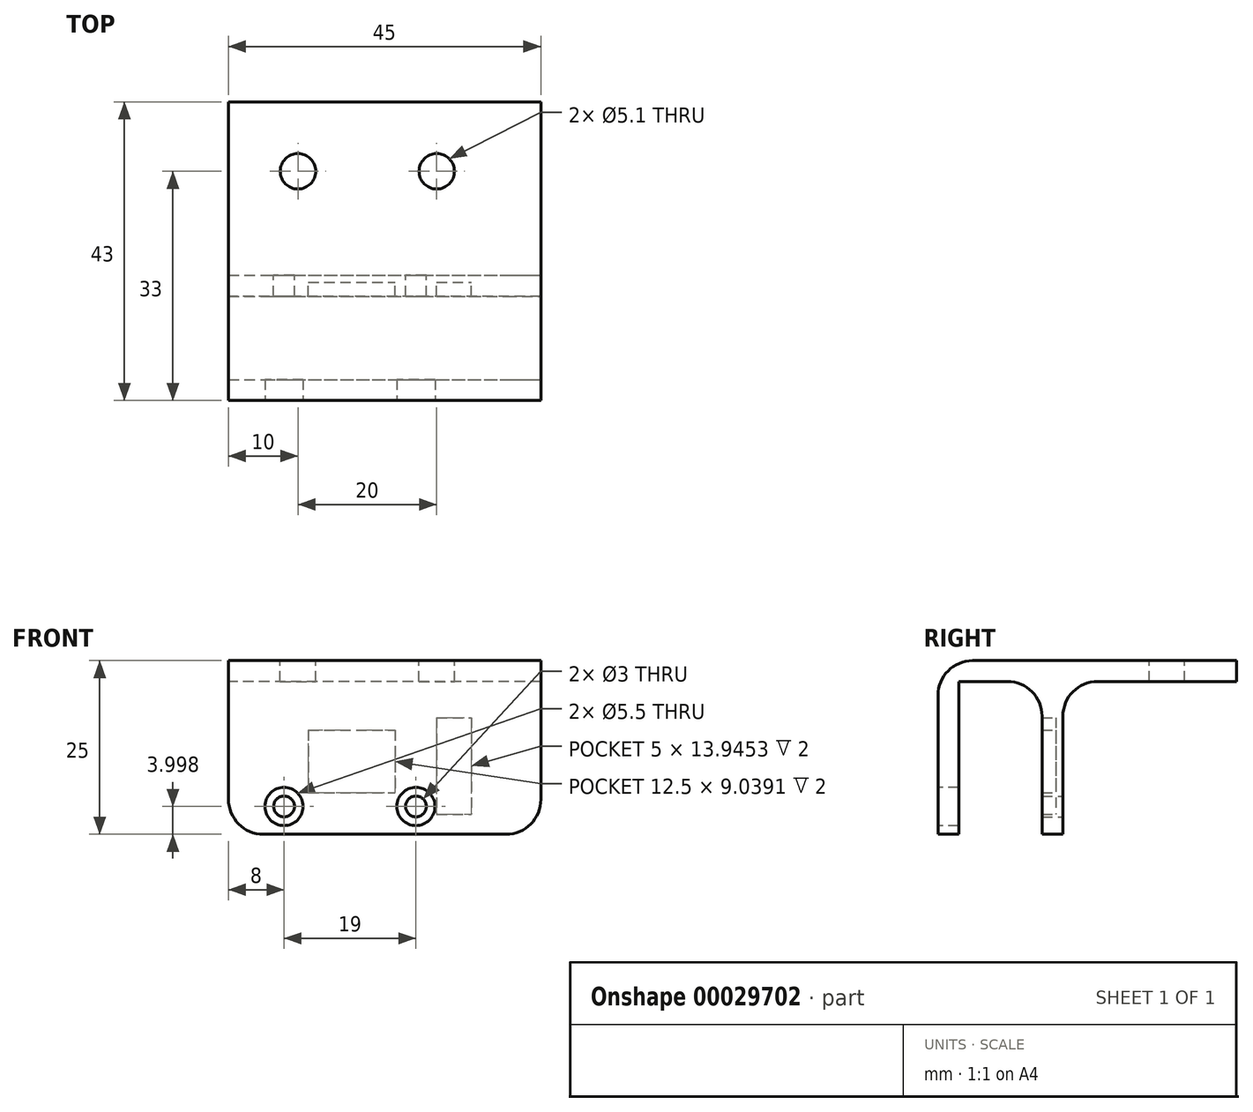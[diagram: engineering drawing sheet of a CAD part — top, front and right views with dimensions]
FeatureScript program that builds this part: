
annotation { "Feature Type Name" : "Feature", "Feature Type Description" : "" }
export const myFeature = defineFeature(function(context is Context, id is Id, definition is map)
    precondition{}
    {
        {
            var Q0;
            Q0=qCreatedBy(makeId("Front.planeOp"),FACE);
            var sketch = newSketch(context, id + "F0", { "sketchPlane" : qUnion([Q0])});
            skLineSegment(sketch, "E0.bottom", {"start": v(-24, 19.03) * mm, "end": v(21, 19.03) * mm});
            skLineSegment(sketch, "E0.top", {"start": v(-24, -5.97) * mm, "end": v(21, -5.97) * mm});
            skLineSegment(sketch, "E0.left", {"start": v(-24, 19.03) * mm, "end": v(-24, -5.97) * mm});
            skLineSegment(sketch, "E0.right", {"start": v(21, 19.03) * mm, "end": v(21, -5.97) * mm});
            skLineSegment(sketch, "E1.bottom", {"start": v(-12.5, 9.03) * mm, "end": v(0, 9.03) * mm});
            skLineSegment(sketch, "E1.top", {"start": v(-12.5, -0.01) * mm, "end": v(0, -0.01) * mm});
            skLineSegment(sketch, "E1.left", {"start": v(-12.5, 9.03) * mm, "end": v(-12.5, -0.01) * mm});
            skLineSegment(sketch, "E1.right", {"start": v(0, 9.03) * mm, "end": v(0, -0.01) * mm});
            skLineSegment(sketch, "E2.bottom", {"start": v(6, 10.83) * mm, "end": v(11, 10.83) * mm});
            skLineSegment(sketch, "E2.top", {"start": v(6, -3.12) * mm, "end": v(11, -3.12) * mm});
            skLineSegment(sketch, "E2.left", {"start": v(6, 10.83) * mm, "end": v(6, -3.12) * mm});
            skLineSegment(sketch, "E2.right", {"start": v(11, 10.83) * mm, "end": v(11, -3.12) * mm});
            skLineSegment(sketch, "E3.top", {"start": v(-24, 16.03) * mm, "end": v(21, 16.03) * mm});
            skLineSegment(sketch, "E3.left", {"start": v(-24, 19.03) * mm, "end": v(-24, 16.03) * mm});
            skLineSegment(sketch, "E3.right", {"start": v(21, 19.03) * mm, "end": v(21, 16.03) * mm});
            skCircle(sketch, "E4", {"center": v(-16, -1.97) * mm, "radius": 1.5 * mm});
            skCircle(sketch, "E5", {"center": v(3, -1.97) * mm, "radius": 1.5 * mm});
            skSolve(sketch);
        }
        {
            var Q0;
            Q0=makeQuery(id+"F0.imprint","IMPRINT",FACE,{"disambiguationData":[TD([[makeQuery(id+"F0.imprint","IMPRINT",EDGE,{"derivedFrom":sQuery(id+"F0.wireOp",EDGE,"E1.bottom")}),-1.0]])]});
            var Q1;
            Q1=makeQuery(id+"F0.imprint","IMPRINT",FACE,{"disambiguationData":[TD([[makeQuery(id+"F0.imprint","IMPRINT",EDGE,{"derivedFrom":sQuery(id+"F0.wireOp",EDGE,"E2.bottom")}),-1.0]])]});
            extrude(context, id + "F1", {"entities" : qUnion([Q0, Q1]), "depth" : 1 * mm});
        }
        {
            var Q0;
            Q0=makeQuery(id+"F0.imprint","IMPRINT",FACE,{"disambiguationData":[TD([[makeQuery(id+"F0.imprint","IMPRINT",EDGE,{"derivedFrom":sQuery(id+"F0.wireOp",EDGE,"E0.top")}),1.0]])]});
            extrude(context, id + "F2", {"entities" : qUnion([Q0]), "operationType" : NewBodyOperationType.ADD, "depth" : 3 * mm});
        }
        {
            var Q0;
            Q0=makeQuery(id+"F0.imprint","IMPRINT",FACE,{"disambiguationData":[TD([[makeQuery(id+"F0.imprint","IMPRINT",EDGE,{"derivedFrom":sQuery(id+"F0.wireOp",EDGE,"E0.bottom")}),-1.0]])]});
            extrude(context, id + "F3", {"entities" : qUnion([Q0]), "oppositeDirection" : true, "depth" : 25 * mm});
        }
        {
            var Q0;
            Q0=makeQuery(id+"F3.opExtrude","CAP_FACE",FACE,{"disambiguationData":[OSD([sQuery(id+"F0.wireOp",EDGE,"E0.bottom"),sQuery(id+"F0.wireOp",EDGE,"E3.top"),sQuery(id+"F0.wireOp",EDGE,"E3.left"),sQuery(id+"F0.wireOp",EDGE,"E3.right")])],"isStart":true});
            extrude(context, id + "F4", {"entities" : qUnion([Q0]), "operationType" : NewBodyOperationType.ADD, "depth" : 3 * mm});
        }
        {
            var Q0;
            {var subQ0=sQuery(id+"F0.wireOp",EDGE,"E0.bottom");Q0=makeQuery(id+"F4.boolean.opBoolean","MERGE",FACE,{"derivedFrom":[makeQuery(id+"F3.opExtrude","SWEPT_FACE",FACE,{"disambiguationData":[OSD([subQ0])]}),makeQuery(id+"F4.opExtrude","SWEPT_FACE",FACE,{"disambiguationData":[OSD([subQ0])]})]});}
            var sketch = newSketch(context, id + "F5", { "sketchPlane" : qUnion([Q0])});
            skCircle(sketch, "E6", {"center": v(-14, 15) * mm, "radius": 2.55 * mm});
            skCircle(sketch, "E7", {"center": v(6, 15) * mm, "radius": 2.55 * mm});
            skSolve(sketch);
        }
        {
            var Q0;
            Q0=makeQuery(id+"F2.opExtrude","CAP_EDGE",EDGE,{"disambiguationData":[OSD([sQuery(id+"F0.wireOp",EDGE,"E3.top")])],"isStart":true});
            var Q1;
            Q1=makeQuery(id+"F3.opExtrude","CAP_EDGE",EDGE,{"disambiguationData":[OSD([sQuery(id+"F0.wireOp",EDGE,"E3.left")])],"isStart":false});
            var Q2;
            Q2=makeQuery(id+"F3.opExtrude","CAP_EDGE",EDGE,{"disambiguationData":[OSD([sQuery(id+"F0.wireOp",EDGE,"E3.right")])],"isStart":false});
            var Q3;
            Q3=makeQuery(id+"F2.opExtrude","SWEPT_EDGE",EDGE,{"disambiguationData":[OSD([sQuery(id+"F0.wireOp",EDGE,"E0.top"),sQuery(id+"F0.wireOp",EDGE,"E0.left")])]});
            var Q4;
            Q4=makeQuery(id+"F2.opExtrude","SWEPT_EDGE",EDGE,{"disambiguationData":[OSD([sQuery(id+"F0.wireOp",EDGE,"E0.top"),sQuery(id+"F0.wireOp",EDGE,"E0.right")])]});
            fillet(context, id + "F6", {"entities" : qUnion([Q0, Q1, Q2, Q3, Q4]), "radius" : 5 * mm, "tangentPropagation" : true, "allowEdgeOverflow" : false});
        }
        {
            var Q0;
            Q0=makeQuery(id+"F5.imprint","IMPRINT",FACE,{"disambiguationData":[TD([[makeQuery(id+"F5.imprint","IMPRINT",EDGE,{"derivedFrom":sQuery(id+"F5.wireOp",EDGE,"E6")}),1.0]])]});
            var Q1;
            Q1=makeQuery(id+"F5.imprint","IMPRINT",FACE,{"disambiguationData":[TD([[makeQuery(id+"F5.imprint","IMPRINT",EDGE,{"derivedFrom":sQuery(id+"F5.wireOp",EDGE,"E7")}),1.0]])]});
            extrude(context, id + "F7", {"entities" : qUnion([Q0, Q1]), "operationType" : NewBodyOperationType.REMOVE, "oppositeDirection" : true, "depth" : 25 * mm});
        }
        {
            var Q0;
            Q0=makeQuery(id+"F0.imprint","IMPRINT",FACE,{"disambiguationData":[TD([[makeQuery(id+"F0.imprint","IMPRINT",EDGE,{"derivedFrom":sQuery(id+"F0.wireOp",EDGE,"E0.bottom")}),-1.0]])]});
            extrude(context, id + "F8", {"entities" : qUnion([Q0]), "operationType" : NewBodyOperationType.ADD, "depth" : 18 * mm});
        }
        {
            var Q0;
            Q0=makeQuery(id+"F8.opExtrude","SWEPT_FACE",FACE,{"disambiguationData":[OSD([sQuery(id+"F0.wireOp",EDGE,"E3.top")])]});
            var sketch = newSketch(context, id + "F9", { "sketchPlane" : qUnion([Q0])});
            skLineSegment(sketch, "E8.bottom", {"start": v(-24, 18) * mm, "end": v(21, 18) * mm});
            skLineSegment(sketch, "E8.top", {"start": v(-24, 15) * mm, "end": v(21, 15) * mm});
            skLineSegment(sketch, "E8.left", {"start": v(-24, 18) * mm, "end": v(-24, 15) * mm});
            skLineSegment(sketch, "E8.right", {"start": v(21, 18) * mm, "end": v(21, 15) * mm});
            skSolve(sketch);
        }
        {
            var Q0;
            Q0 = qSketchRegion(id + "F9", true);
            extrude(context, id + "F10", {"entities" : qUnion([Q0]), "operationType" : NewBodyOperationType.ADD, "depth" : 22 * mm});
        }
        {
            var Q0;
            Q0=makeQuery(id+"F10.boolean.opBoolean","MERGE",FACE,{"derivedFrom":[makeQuery(id+"F8.opExtrude","CAP_FACE",FACE,{"disambiguationData":[OSD([sQuery(id+"F0.wireOp",EDGE,"E0.bottom"),sQuery(id+"F0.wireOp",EDGE,"E3.top"),sQuery(id+"F0.wireOp",EDGE,"E3.left"),sQuery(id+"F0.wireOp",EDGE,"E3.right")])],"isStart":false}),makeQuery(id+"F10.opExtrude","SWEPT_FACE",FACE,{"disambiguationData":[OSD([sQuery(id+"F9.wireOp",EDGE,"E8.bottom")])]})]});
            var sketch = newSketch(context, id + "F11", { "sketchPlane" : qUnion([Q0])});
            skCircle(sketch, "E9", {"center": v(-16, -1.97) * mm, "radius": 2.75 * mm});
            skCircle(sketch, "E10", {"center": v(3, -1.97) * mm, "radius": 2.75 * mm});
            skSolve(sketch);
        }
        {
            var Q0;
            Q0=makeQuery(id+"F11.imprint","IMPRINT",FACE,{"disambiguationData":[TD([[makeQuery(id+"F11.imprint","IMPRINT",EDGE,{"derivedFrom":sQuery(id+"F11.wireOp",EDGE,"E9")}),1.0]])]});
            var Q1;
            Q1=makeQuery(id+"F11.imprint","IMPRINT",FACE,{"disambiguationData":[TD([[makeQuery(id+"F11.imprint","IMPRINT",EDGE,{"derivedFrom":sQuery(id+"F11.wireOp",EDGE,"E10")}),1.0]])]});
            var Q2;
            Q2=makeQuery(id+"F10.opExtrude","SWEPT_FACE",FACE,{"disambiguationData":[OSD([sQuery(id+"F9.wireOp",EDGE,"E8.top")])]});
            extrude(context, id + "F12", {"entities" : qUnion([Q0, Q1]), "operationType" : NewBodyOperationType.REMOVE, "endBound" : BoundingType.UP_TO_SURFACE, "oppositeDirection" : true, "endBoundEntityFace" : qUnion([Q2]), "depth" : 16 * mm});
        }
        {
            var Q0;
            Q0=makeQuery(id+"F10.opExtrude","CAP_EDGE",EDGE,{"disambiguationData":[OSD([sQuery(id+"F9.wireOp",EDGE,"E8.left")])],"isStart":false});
            var Q1;
            Q1=makeQuery(id+"F10.opExtrude","CAP_EDGE",EDGE,{"disambiguationData":[OSD([sQuery(id+"F9.wireOp",EDGE,"E8.right")])],"isStart":false});
            fillet(context, id + "F13", {"entities" : qUnion([Q0, Q1]), "radius" : 5 * mm, "tangentPropagation" : true, "allowEdgeOverflow" : false});
        }
        {
            var Q0;
            Q0=makeQuery(id+"F8.opExtrude","CAP_EDGE",EDGE,{"disambiguationData":[OSD([sQuery(id+"F0.wireOp",EDGE,"E0.bottom")])],"isStart":false});
            var Q1;
            Q1=makeQuery(id+"F10.opExtrude","CAP_EDGE",EDGE,{"disambiguationData":[OSD([sQuery(id+"F9.wireOp",EDGE,"E8.top")])],"isStart":true});
            var Q2;
            {var subQ0=sQuery(id+"F0.wireOp",EDGE,"E3.top");Q2=makeQuery(id+"F8.boolean.opBoolean","INTERSECT",EDGE,{"derivedFrom":[makeQuery(id+"F4.boolean.opBoolean","MERGE",FACE,{"derivedFrom":[makeQuery(id+"F2.opExtrude","CAP_FACE",FACE,{"disambiguationData":[OSD([sQuery(id+"F0.wireOp",EDGE,"E0.top"),sQuery(id+"F0.wireOp",EDGE,"E0.left"),sQuery(id+"F0.wireOp",EDGE,"E0.right"),sQuery(id+"F0.wireOp",EDGE,"E1.bottom"),sQuery(id+"F0.wireOp",EDGE,"E1.top"),sQuery(id+"F0.wireOp",EDGE,"E1.left"),sQuery(id+"F0.wireOp",EDGE,"E1.right"),sQuery(id+"F0.wireOp",EDGE,"E2.bottom"),sQuery(id+"F0.wireOp",EDGE,"E2.top"),sQuery(id+"F0.wireOp",EDGE,"E2.left"),sQuery(id+"F0.wireOp",EDGE,"E2.right"),subQ0,sQuery(id+"F0.wireOp",EDGE,"E4"),sQuery(id+"F0.wireOp",EDGE,"E5")])],"isStart":false}),makeQuery(id+"F4.opExtrude","CAP_FACE",FACE,{"disambiguationData":[OSD([sQuery(id+"F0.wireOp",EDGE,"E0.bottom"),subQ0,sQuery(id+"F0.wireOp",EDGE,"E3.left"),sQuery(id+"F0.wireOp",EDGE,"E3.right")])],"isStart":false})]}),makeQuery(id+"F8.opExtrude","SWEPT_FACE",FACE,{"disambiguationData":[OSD([subQ0])]})]});}
            fillet(context, id + "F14", {"entities" : qUnion([Q0, Q1, Q2]), "radius" : 5 * mm, "tangentPropagation" : true, "allowEdgeOverflow" : false});
        }
    });
